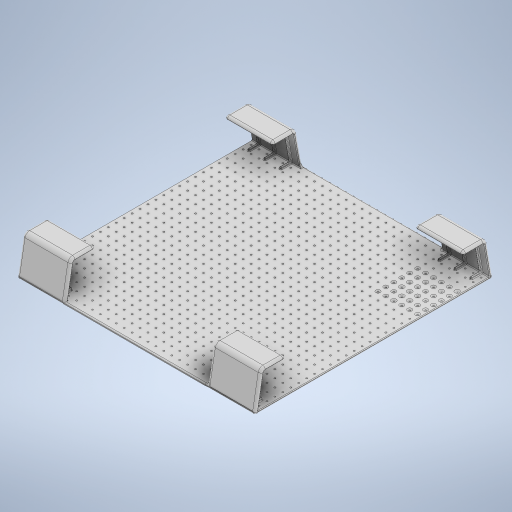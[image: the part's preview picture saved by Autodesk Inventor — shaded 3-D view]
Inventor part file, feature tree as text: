
AUTODESK INVENTOR PART (.ipt)
format: ipt  version: 2023 (Build 270158030, 158C)  size: 2,921,984 bytes
history: native  units: mm
features: fillet x9, extrude x5, sketch x4, plane x3, mirror x2, pattern_linear x1
ambient origin geometry x8: Origin, YZ Plane, XZ Plane, XY Plane, X Axis, Y Axis, Z Axis, Center Point
bodies: Solid1 (feature_tree)
feature tree (24):
  extrude  "Extrusion1"  Depth=150.0mm
  extrude  "Extrusion2"  Depth=1.5mm
  extrude  "Extrusion4"  Depth=120.0mm
  plane  "Work Plane1"
  extrude  "Extrusion5"  Depth=1.0mm TaperAngle=0.0deg
  fillet  "Fillet8"  Radius=1.0mm
  pattern_linear  "Rectangular Pattern1"  Spacing1=2.5mm  [1 undecoded]
  fillet  "Fillet13"  Radius=5.0mm
  fillet  "Fillet14"  Radius=300.0mm
  fillet  "Fillet15"  Radius=2.5mm
  plane  "Work Plane2"
  mirror  "Mirror1"
  plane  "Work Plane4"
  mirror  "Mirror3"
  fillet  "Fillet16"  Radius=5.0mm
  fillet  "Fillet17"  Radius=20.0mm
  fillet  "Fillet18"  Radius=2.0mm
  fillet  "Fillet19"  Radius=2.0mm
  extrude  "Extrusion3"  Depth=1.0mm
  fillet  "Fillet20"  Radius=15.0mm
  sketch  "Sketch1"  dims[d0=150.0mm d1=150.0mm]
  sketch  "Sketch3"  dims[d2=1.5mm d3=0.0mm d4=3.0mm]
  sketch  "Sketch4"  dims[d5=90.0deg d6=120.0mm]
  sketch  "Sketch7"  dims[d7=90.0deg d8=3.0mm d9=0.0mm d10=1.0mm d11=2.5mm d12=5.0mm d13=300.0mm d15=5.0mm d16=300.0mm d18=5.0mm d21=2.5mm d23=5.0mm d24=0.0mm d29=20.0mm d30=2.0mm d31=2.0mm d32=13.962634mm d33=15.0mm d34=2.0mm d35=2.0mm d36=13.962634mm d37=15.0mm d41=30.0mm d42=30.0mm d43=10.0mm d44=10.0mm d45=1.5mm d46=0.0mm d48=6.0mm d49=1.3mm d50=1.3mm d51=1.3mm d52=7.0mm d53=-5.0mm d54=1.0mm d55=0.0mm d56=0.45mm d61=30.0mm d63=10.0mm d64=0.4mm d65=0.4mm d66=0.39mm d67=3.0mm d68=1.5mm d69=0.4mm d70=1.0mm d71=1.0mm d27=0.0mm d28=0.0mm]
note: 1 required parameter value undecoded (feature->parameter linkage not recoverable at this tier; creation-order binding heuristic only, values carry confidence <= 0.55)
